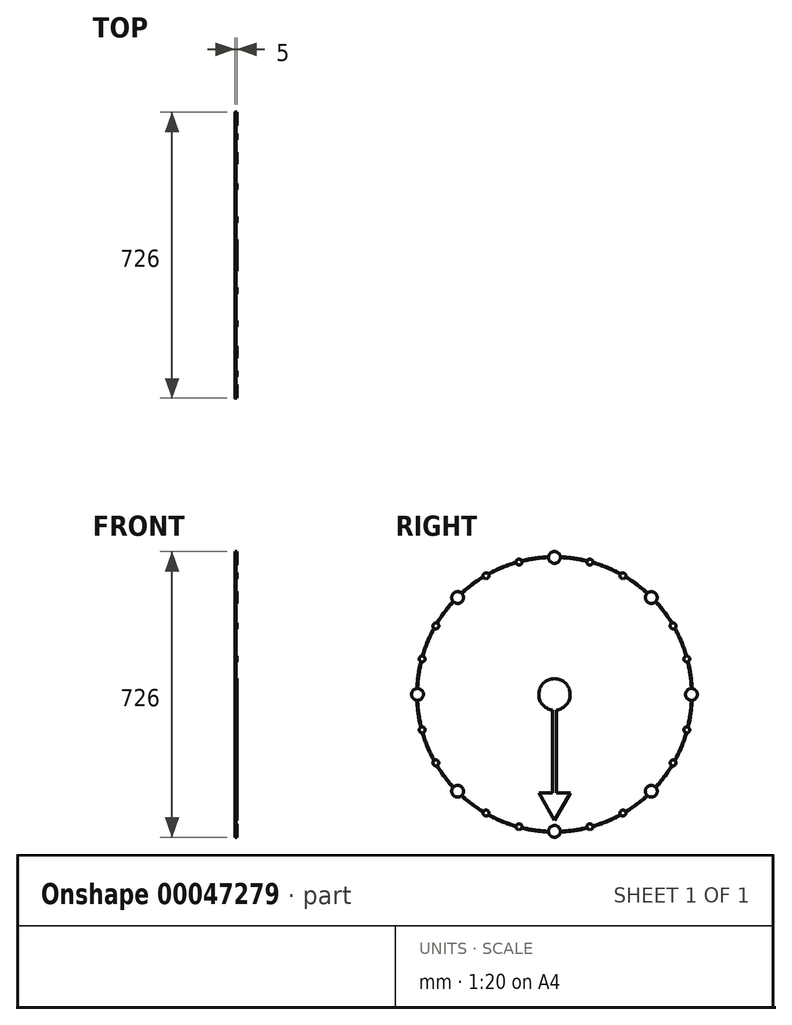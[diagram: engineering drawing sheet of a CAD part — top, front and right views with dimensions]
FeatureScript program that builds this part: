
annotation { "Feature Type Name" : "Feature", "Feature Type Description" : "" }
export const myFeature = defineFeature(function(context is Context, id is Id, definition is map)
    precondition{}
    {
        {
            var Q0;
            Q0=qCreatedBy(makeId("Top.planeOp"),FACE);
            var sketch = newSketch(context, id + "F0", { "sketchPlane" : qUnion([Q0])});
            skLineSegment(sketch, "E0", {"start": v(15.52, 0) * mm, "end": v(300.4, 0) * mm, "construction": true});
            skSolve(sketch);
        }
        {
            var Q0;
            Q0=qCreatedBy(makeId("Right.planeOp"),FACE);
            var sketch = newSketch(context, id + "F1", { "sketchPlane" : qUnion([Q0])});
            skCircle(sketch, "E1", {"center": v(0, 0) * mm, "radius": 350 * mm});
            skCircle(sketch, "E2", {"center": v(0, 0) * mm, "radius": 348 * mm});
            skSolve(sketch);
        }
        {
            var Q0;
            Q0 = qSketchRegion(id + "F1", true);
            extrude(context, id + "F2", {"entities" : qUnion([Q0]), "depth" : 2 * mm});
        }
        {
            var Q0;
            Q0=qCreatedBy(makeId("Right.planeOp"),FACE);
            var sketch = newSketch(context, id + "F3", { "sketchPlane" : qUnion([Q0])});
            skCircle(sketch, "E3", {"center": v(0, -348) * mm, "radius": 7.5 * mm});
            skSolve(sketch);
        }
        {
            var Q0;
            Q0 = qSketchRegion(id + "F3", true);
            extrude(context, id + "F4", {"entities" : qUnion([Q0]), "depth" : 5 * mm});
        }
        {
            var Q0;
            Q0=makeQuery(id+"F4.opExtrude","SWEPT_BODY",BODY,{"disambiguationData":[OSD([sQuery(id+"F3.wireOp",EDGE,"E3")])]});
            var Q1;
            Q1=sQuery(id+"F0.wireOp",EDGE,"E0");
            circularPattern(context, id + "F5", {"operationType" : NewBodyOperationType.ADD, "entities" : qUnion([Q0]), "axis" : qUnion([Q1]), "angle" : 360 * degree, "instanceCount" : 24, "equalSpace" : true});
        }
        {
            var Q0;
            Q0=qCreatedBy(makeId("Right.planeOp"),FACE);
            var sketch = newSketch(context, id + "F6", { "sketchPlane" : qUnion([Q0])});
            skCircle(sketch, "E4", {"center": v(0, -348) * mm, "radius": 15 * mm});
            skSolve(sketch);
        }
        {
            var Q0;
            Q0=makeQuery(id+"F6.imprint","IMPRINT",FACE,{"disambiguationData":[TD([[makeQuery(id+"F6.imprint","IMPRINT",EDGE,{"derivedFrom":sQuery(id+"F6.wireOp",EDGE,"E4")}),1.0]])]});
            extrude(context, id + "F7", {"entities" : qUnion([Q0]), "depth" : 5 * mm});
        }
        {
            var Q0;
            Q0=makeQuery(id+"F7.opExtrude","SWEPT_BODY",BODY,{"disambiguationData":[OSD([sQuery(id+"F6.wireOp",EDGE,"E4")])]});
            var Q1;
            Q1=sQuery(id+"F0.wireOp",EDGE,"E0");
            circularPattern(context, id + "F8", {"operationType" : NewBodyOperationType.ADD, "entities" : qUnion([Q0]), "axis" : qUnion([Q1]), "angle" : 360 * degree, "instanceCount" : 8, "equalSpace" : true});
        }
        {
            var Q0;
            Q0=qCreatedBy(makeId("Right.planeOp"),FACE);
            var sketch = newSketch(context, id + "F9", { "sketchPlane" : qUnion([Q0])});
            skArc(sketch, "E5", {"start": v(5, -39.69) * mm, "mid": v(0, 40) * mm, "end": v(-5, -39.69) * mm});
            skLineSegment(sketch, "E6.left", {"start": v(-5, -39.69) * mm, "end": v(-5, -250.72) * mm});
            skLineSegment(sketch, "E6.right", {"start": v(5, -39.69) * mm, "end": v(5, -250.72) * mm});
            skLineSegment(sketch, "E7", {"start": v(0, -320) * mm, "end": v(-40, -250.72) * mm});
            skLineSegment(sketch, "E8", {"start": v(-40, -250.72) * mm, "end": v(-5, -250.72) * mm});
            skLineSegment(sketch, "E9", {"start": v(40, -250.72) * mm, "end": v(0, -320) * mm});
            skLineSegment(sketch, "E10.trimOffspring", {"start": v(5, -250.72) * mm, "end": v(40, -250.72) * mm});
            skLineSegment(sketch, "E11", {"start": v(0, -320) * mm, "end": v(0, 0) * mm, "construction": true});
            skSolve(sketch);
        }
        {
            var Q0;
            Q0 = qSketchRegion(id + "F9", true);
            extrude(context, id + "F10", {"entities" : qUnion([Q0]), "depth" : 5 * mm});
        }
    });
